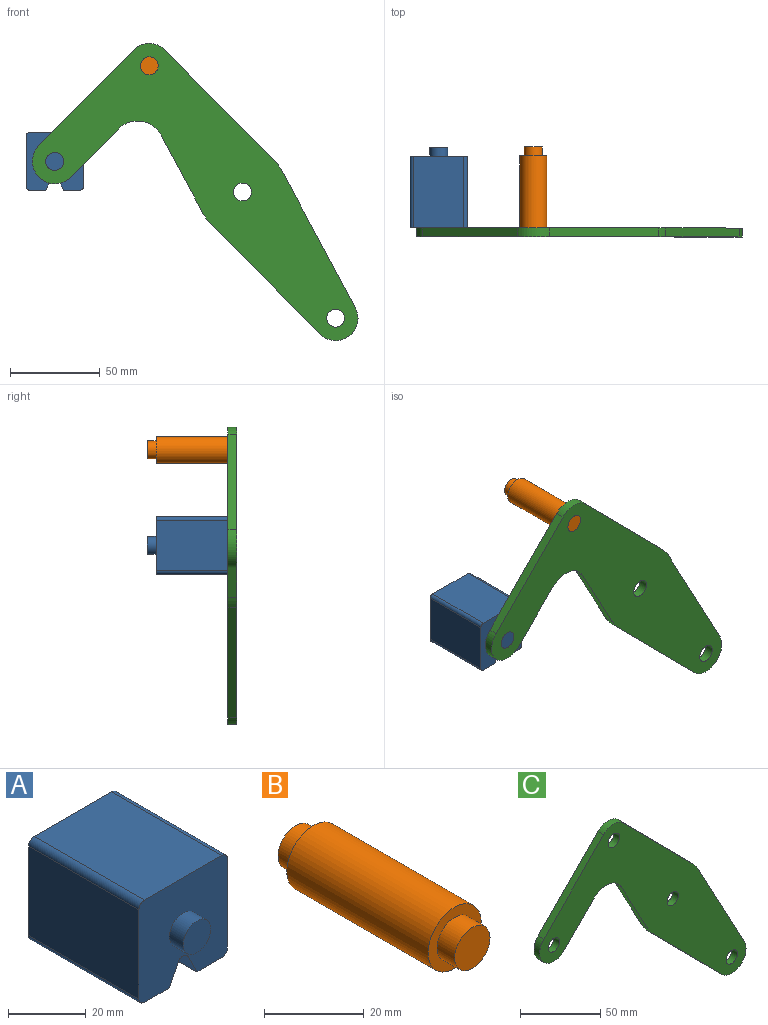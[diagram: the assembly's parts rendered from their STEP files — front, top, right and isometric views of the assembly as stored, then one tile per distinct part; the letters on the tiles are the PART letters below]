
ASSEMBLY  parts=3 mates=1
PART A: 18 faces, bbox 32.1x50x32.1 mm
  f0: plane 40x28.08mm, normal (1,0,0), area 1123.1mm2, adj f4,f10,f13,f14
  f1: plane 40x9.04mm, normal (0,0,-1), area 361.6mm2, adj f2,f4,f10,f14
  f2: plane 40x6.42mm, normal (-0.89,0,-0.45), area 287.2mm2, adj f1,f4,f10,f15
  f3: plane 40x6.42mm, normal (0.89,0,-0.45), area 287.2mm2, adj f4,f5,f10,f15
  f4: plane 32.08x32.08mm, normal (0,-1,0), area 900.6mm2, adj f0,f1,f2,f3,f5,f6,f7,f9
  f5: plane 40x9.04mm, normal (0,0,-1), area 361.6mm2, adj f3,f4,f10,f16
  f6: plane 40x28.08mm, normal (0,0,1), area 1123.1mm2, adj f4,f10,f13,f17
  f7: plane 40x28.08mm, normal (-1,0,0), area 1123.1mm2, adj f4,f10,f16,f17
  f8: plane 10x10mm, normal (0,-1,0), area 78.5mm2, adj f9
  f9: cylinder r=5mm len=10mm, axis (0,1,0), area 157.1mm2, adj f4,f8
  f10: plane 32.08x32.08mm, normal (0,1,0), area 900.6mm2, adj f0,f1,f2,f3,f5,f6,f7,f12
  f11: plane 10x10mm, normal (0,1,0), area 78.5mm2, adj f12
  f12: cylinder r=5mm len=10mm, axis (0,-1,0), area 157.1mm2, adj f10,f11
  f13: cylinder r=2mm len=40mm, axis (0,1,0), area 125.7mm2, adj f0,f4,f6,f10
  f14: cylinder r=2mm len=40mm, axis (0,-1,0), area 125.7mm2, adj f0,f1,f4,f10
  f15: cylinder r=2mm len=40mm, axis (0,1,0), area 177.1mm2, adj f2,f3,f4,f10
  f16: cylinder r=2mm len=40mm, axis (0,1,0), area 125.7mm2, adj f4,f5,f7,f10
  f17: cylinder r=2mm len=40mm, axis (0,-1,0), area 125.7mm2, adj f4,f6,f7,f10
PART B: 7 faces, bbox 15x50x15 mm
  f0: cylinder r=7.5mm len=40mm, axis (0,-1,0), area 1885mm2, adj f2,f5
  f1: cylinder r=5mm len=10mm, axis (0,1,0), area 157.1mm2, adj f2,f3
  f2: plane 15x15mm, normal (0,-1,0), area 98.2mm2, adj f0,f1
  f3: plane 10x10mm, normal (0,-1,0), area 78.5mm2, adj f1
  f4: cylinder r=5mm len=10mm, axis (0,-1,0), area 157.1mm2, adj f5,f6
  f5: plane 15x15mm, normal (0,1,0), area 98.2mm2, adj f0,f4
  f6: plane 10x10mm, normal (0,1,0), area 78.5mm2, adj f4
PART C: 18 faces, bbox 181.7x5x165.8 mm
  f0: plane 43.49x23.35mm, normal (-0.88,0,-0.47), area 246.8mm2, adj f1,f14,f16,f17
  f1: cylinder r=25mm len=5.75mm, axis (0,1,0), area 35.8mm2, adj f0,f2,f16,f17
  f2: plane 61.6x60.87mm, normal (-0.71,0,-0.7), area 433mm2, adj f1,f3,f16,f17
  f3: cylinder r=12.5mm len=21.39mm, axis (0,1,0), area 178.4mm2, adj f2,f4,f16,f17
  f4: plane 76.3x40.96mm, normal (0.88,0,0.47), area 433mm2, adj f3,f5,f16,f17
  f5: cylinder r=25mm len=5.75mm, axis (0,1,0), area 35.8mm2, adj f4,f6,f16,f17
  f6: plane 61.6x60.87mm, normal (0.71,0,0.7), area 433mm2, adj f5,f7,f16,f17
  f7: cylinder r=12.5mm len=17.78mm, axis (0,1,0), area 98.9mm2, adj f6,f8,f16,f17
  f8: plane 53.35x52.71mm, normal (-0.71,0,0.7), area 375mm2, adj f7,f9,f16,f17
  f9: cylinder r=12.5mm len=21.39mm, axis (0,1,0), area 196.3mm2, adj f8,f10,f16,f17
  f10: plane 26.86x26.54mm, normal (0.71,0,-0.7), area 188.8mm2, adj f9,f14,f16,f17
  f11: cylinder r=5mm len=10mm, axis (0,1,0), area 157.1mm2, adj f16,f17
  f12: cylinder r=5mm len=10mm, axis (0,1,0), area 157.1mm2, adj f16,f17
  f13: cylinder r=5mm len=10mm, axis (0,1,0), area 157.1mm2, adj f16,f17
  f14: cylinder r=15mm len=23.89mm, axis (0,1,0), area 140.2mm2, adj f0,f10,f16,f17
  f15: cylinder r=5mm len=10mm, axis (0,1,0), area 157.1mm2, adj f16,f17
  f16: plane 181.66x165.78mm, normal (0,-1,0), area 8710.1mm2, adj f0,f1,f2,f3,f4,f5,f6,f7
  f17: plane 181.66x165.78mm, normal (0,1,0), area 8710.1mm2, adj f0,f1,f2,f3,f4,f5,f6,f7
PLACE A t=(0,-20,0)mm
PLACE B t=(0,-20,0)mm
PLACE C t=(0,-20,0)mm
MATE revolute C.f9 <-> A.f9  axis (0,1,0) through (-104.69,-20,17.04)mm
